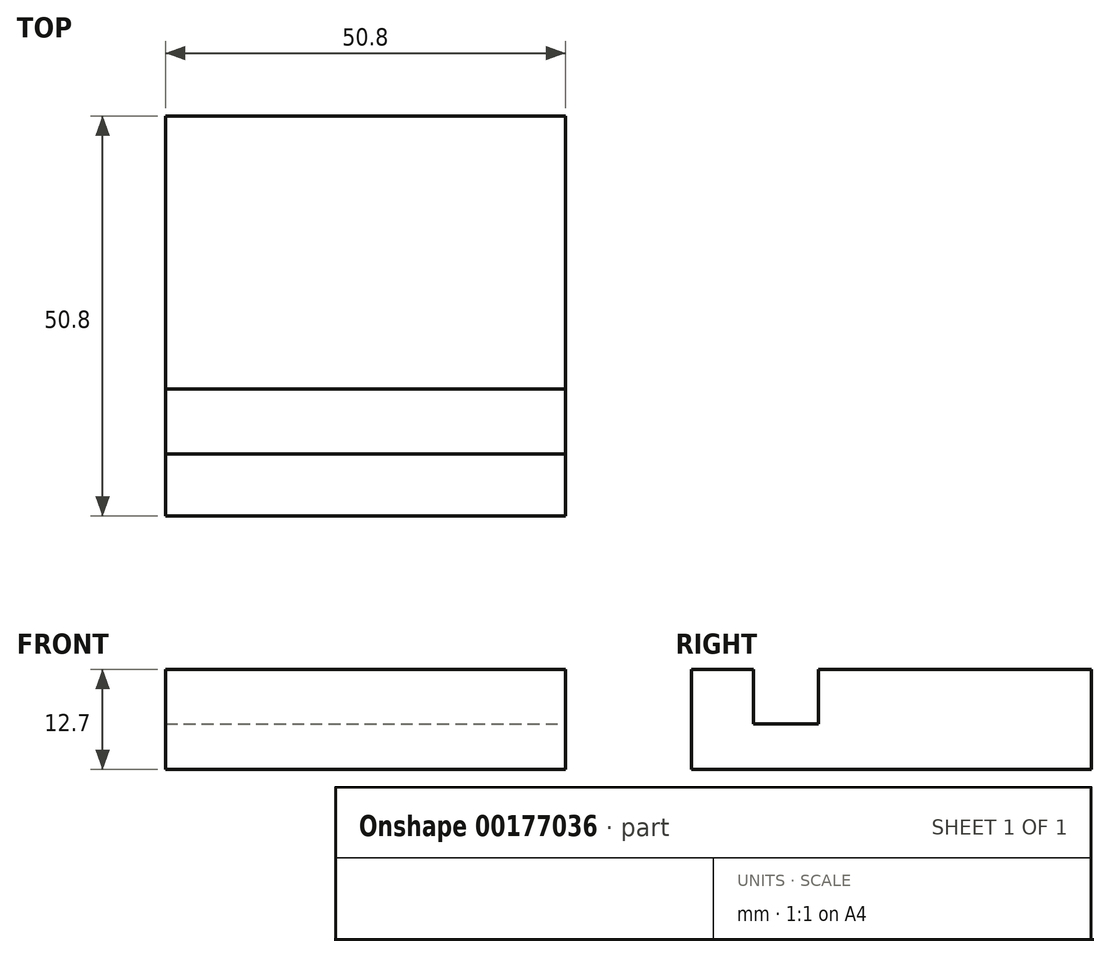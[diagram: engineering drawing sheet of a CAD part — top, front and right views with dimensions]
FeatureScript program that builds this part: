
annotation { "Feature Type Name" : "Feature", "Feature Type Description" : "" }
export const myFeature = defineFeature(function(context is Context, id is Id, definition is map)
    precondition{}
    {
        {
            var Q0;
            Q0=qCreatedBy(makeId("Right.planeOp"),FACE);
            var sketch = newSketch(context, id + "F0", { "sketchPlane" : qUnion([Q0])});
            skLineSegment(sketch, "E0.bottom", {"start": v(25.4, 6.35) * mm, "end": v(-25.4, 6.35) * mm});
            skLineSegment(sketch, "E0.top", {"start": v(25.4, -6.35) * mm, "end": v(-25.4, -6.35) * mm});
            skLineSegment(sketch, "E0.left", {"start": v(25.4, 6.35) * mm, "end": v(25.4, -6.35) * mm});
            skLineSegment(sketch, "E0.right", {"start": v(-25.4, 6.35) * mm, "end": v(-25.4, -6.35) * mm});
            skPoint(sketch, "E0.middle", {"position": v(0, 0) * mm});
            skSolve(sketch);
        }
        {
            var Q0;
            Q0=makeQuery(id+"F0.imprint","IMPRINT",FACE,{"disambiguationData":[TD([[makeQuery(id+"F0.imprint","IMPRINT",EDGE,{"derivedFrom":sQuery(id+"F0.wireOp",EDGE,"E0.bottom")}),1.0]])]});
            extrude(context, id + "F1", {"entities" : qUnion([Q0]), "depth" : 25.4 * mm, "hasSecondDirection" : true, "secondDirectionOppositeDirection" : true, "secondDirectionDepth" : 25.4 * mm});
        }
        {
            var Q0;
            Q0=makeQuery(id+"F1.opExtrude","CAP_FACE",FACE,{"disambiguationData":[OSD([sQuery(id+"F0.wireOp",EDGE,"E0.bottom"),sQuery(id+"F0.wireOp",EDGE,"E0.top"),sQuery(id+"F0.wireOp",EDGE,"E0.left"),sQuery(id+"F0.wireOp",EDGE,"E0.right")])],"isStart":false});
            var sketch = newSketch(context, id + "F2", { "sketchPlane" : qUnion([Q0])});
            skLineSegment(sketch, "E1.bottom", {"start": v(-17.52, 8.36) * mm, "end": v(-9.27, 8.36) * mm});
            skLineSegment(sketch, "E1.top", {"start": v(-17.52, -0.57) * mm, "end": v(-9.27, -0.57) * mm});
            skLineSegment(sketch, "E1.left", {"start": v(-17.52, 8.36) * mm, "end": v(-17.52, -0.57) * mm});
            skLineSegment(sketch, "E1.right", {"start": v(-9.27, 8.36) * mm, "end": v(-9.27, -0.57) * mm});
            skLineSegment(sketch, "E2", {"start": v(-14.5, 9.8) * mm, "end": v(-17.52, 1.52) * mm, "construction": true});
            skLineSegment(sketch, "E3", {"start": v(-17.52, 1.52) * mm, "end": v(-11.8, -0.57) * mm, "construction": true});
            skLineSegment(sketch, "E4", {"start": v(-8.02, 9.8) * mm, "end": v(-14.5, 9.8) * mm, "construction": true});
            skPoint(sketch, "E5", {"position": v(-9.27, 6.35) * mm});
            skLineSegment(sketch, "E6", {"start": v(-11.8, -0.57) * mm, "end": v(-9.27, 6.35) * mm, "construction": true});
            skLineSegment(sketch, "E7", {"start": v(-9.27, 6.35) * mm, "end": v(-8.02, 9.8) * mm, "construction": true});
            skSolve(sketch);
        }
        {
            var Q0;
            Q0 = qSketchRegion(id + "F2", true);
            extrude(context, id + "F3", {"entities" : qUnion([Q0]), "operationType" : NewBodyOperationType.REMOVE, "oppositeDirection" : true, "depth" : 50.8 * mm});
        }
    });
